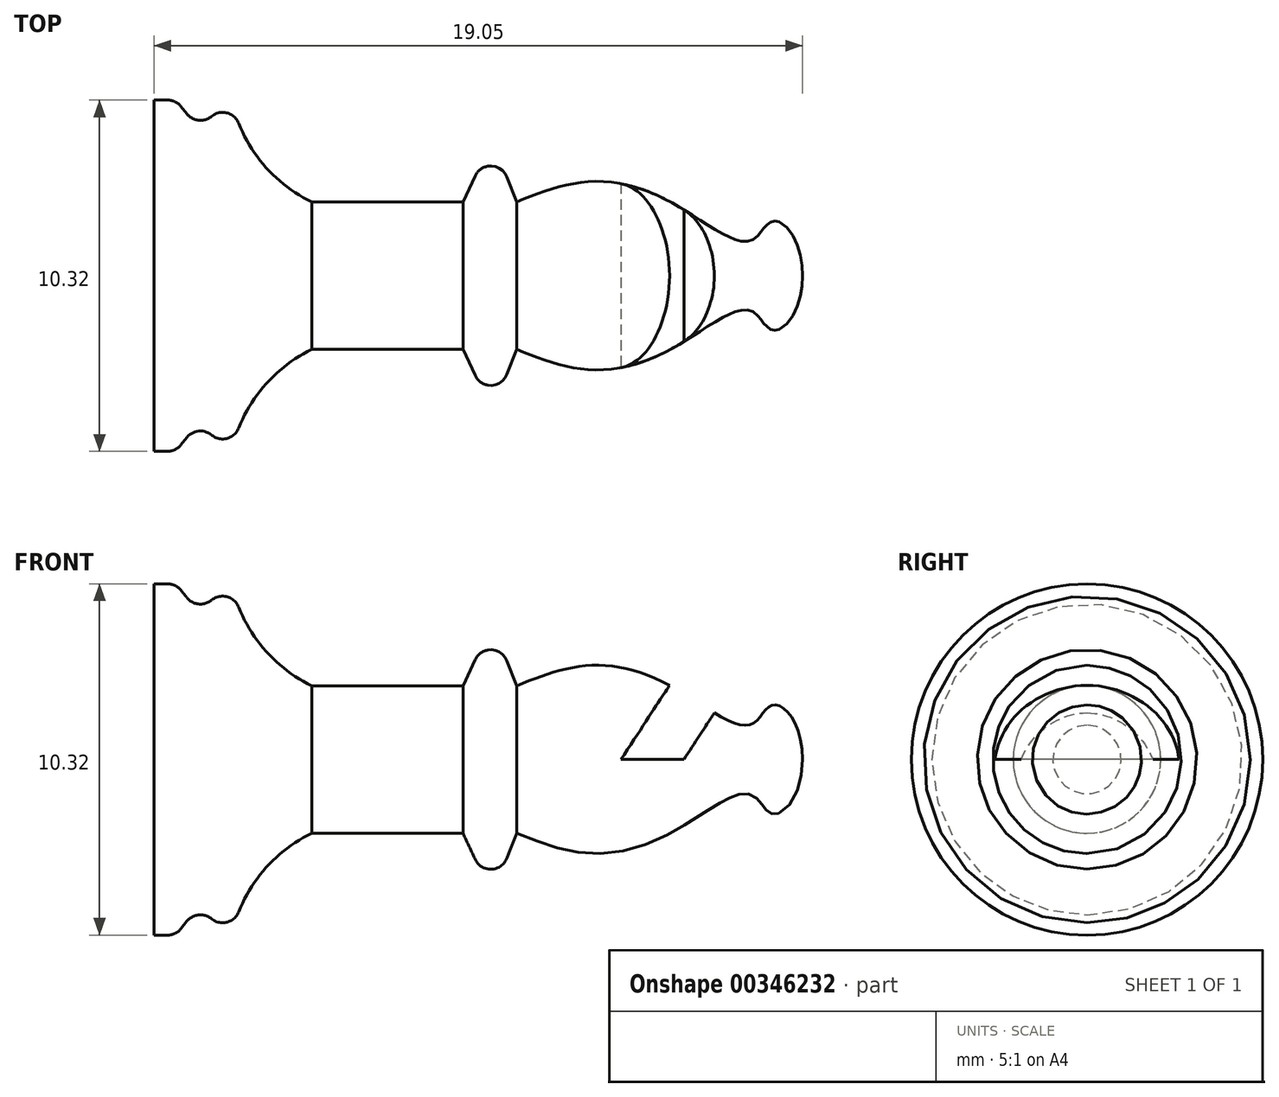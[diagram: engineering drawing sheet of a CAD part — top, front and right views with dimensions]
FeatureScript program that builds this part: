
annotation { "Feature Type Name" : "Feature", "Feature Type Description" : "" }
export const myFeature = defineFeature(function(context is Context, id is Id, definition is map)
    precondition{}
    {
        {
            var Q0;
            Q0=qCreatedBy(makeId("Front.planeOp"),FACE);
            var sketch = newSketch(context, id + "F0", { "sketchPlane" : qUnion([Q0])});
            skLineSegment(sketch, "E0", {"start": v(0, 0) * mm, "end": v(-19.05, 0) * mm});
            skLineSegment(sketch, "E1", {"start": v(-19.05, 0) * mm, "end": v(-19.05, 5.16) * mm});
            skLineSegment(sketch, "E2", {"start": v(-19.05, 5.16) * mm, "end": v(-18.41, 5.16) * mm});
            skLineSegment(sketch, "E3", {"start": v(-18.41, 5.16) * mm, "end": v(-17.76, 4.36) * mm});
            skLineSegment(sketch, "E4", {"start": v(-17.76, 4.36) * mm, "end": v(-16.77, 5.16) * mm});
            skArc(sketch, "E5", {"start": v(-16.77, 5.16) * mm, "mid": v(-15.94, 3.4) * mm, "end": v(-14.42, 2.17) * mm});
            skLineSegment(sketch, "E6", {"start": v(-14.42, 2.17) * mm, "end": v(-9.97, 2.17) * mm});
            skLineSegment(sketch, "E7", {"start": v(-9.97, 2.17) * mm, "end": v(-9.12, 4) * mm});
            skLineSegment(sketch, "E8", {"start": v(-9.12, 4) * mm, "end": v(-8.39, 2.17) * mm});
            skFitSpline(sketch, "E9", {"points": [v(-8.39, 2.17) * mm, v(-6.38, 2.76) * mm, v(-3.88, 2.17) * mm, v(-1.54, 1.02) * mm, v(-0.9, 1.6) * mm, v(0, 0) * mm], "startDerivative": vector(9.4, 3.76) * mm, "endDerivative": vector(0, -16.76) * mm});
            skSolve(sketch);
        }
        {
            var Q0;
            Q0=makeQuery(id+"F0.imprint","IMPRINT",FACE,{"disambiguationData":[TD([[makeQuery(id+"F0.imprint","IMPRINT",EDGE,{"derivedFrom":sQuery(id+"F0.wireOp",EDGE,"E0")}),-1.0]])]});
            var Q1;
            Q1=sQuery(id+"F0.wireOp",EDGE,"E0");
            revolve(context, id + "F1", {"entities" : qUnion([Q0]), "axis" : qUnion([Q1]), "revolveType" : RevolveType.FULL});
        }
        {
            var Q0;
            Q0=makeQuery(id+"F1.opRevolve","SWEPT_EDGE",EDGE,{"disambiguationData":[OSD([sQuery(id+"F0.wireOp",EDGE,"E7"),sQuery(id+"F0.wireOp",EDGE,"E8")])]});
            var Q1;
            Q1=makeQuery(id+"F1.opRevolve","SWEPT_EDGE",EDGE,{"disambiguationData":[OSD([sQuery(id+"F0.wireOp",EDGE,"AUx2sYwA-PIeI-d8Dh-zgte-X192royZ0Wcn"),sQuery(id+"F0.wireOp",EDGE,"91591d6d-3b99-44fd-bbde-36bfa9a7b408")])]});
            var Q2;
            Q2=makeQuery(id+"F1.opRevolve","SWEPT_EDGE",EDGE,{"disambiguationData":[OSD([sQuery(id+"F0.wireOp",EDGE,"E4"),sQuery(id+"F0.wireOp",EDGE,"E5")])]});
            var Q3;
            Q3=makeQuery(id+"F1.opRevolve","SWEPT_EDGE",EDGE,{"disambiguationData":[OSD([sQuery(id+"F0.wireOp",EDGE,"E2"),sQuery(id+"F0.wireOp",EDGE,"E3")])]});
            var Q4;
            Q4=makeQuery(id+"F1.opRevolve","SWEPT_EDGE",EDGE,{"disambiguationData":[OSD([sQuery(id+"F0.wireOp",EDGE,"E3"),sQuery(id+"F0.wireOp",EDGE,"E4")])]});
            fillet(context, id + "F2", {"entities" : qUnion([Q0, Q1, Q2, Q3, Q4]), "radius" : 0.5 * mm, "tangentPropagation" : true, "allowEdgeOverflow" : false});
        }
        {
            var Q0;
            Q0=qCreatedBy(makeId("Front.planeOp"),FACE);
            var sketch = newSketch(context, id + "F3", { "sketchPlane" : qUnion([Q0])});
            skLineSegment(sketch, "E10", {"start": v(-5.33, 0) * mm, "end": v(-3.23, 3.22) * mm});
            skLineSegment(sketch, "E11", {"start": v(-3.23, 3.22) * mm, "end": v(-1.93, 2.37) * mm});
            skLineSegment(sketch, "E12", {"start": v(-1.93, 2.37) * mm, "end": v(-3.49, 0) * mm});
            skLineSegment(sketch, "E13", {"start": v(-3.49, 0) * mm, "end": v(-5.33, 0) * mm});
            skSolve(sketch);
        }
        {
            var Q0;
            Q0=makeQuery(id+"F3.imprint","IMPRINT",FACE,{"disambiguationData":[TD([[makeQuery(id+"F3.imprint","IMPRINT",EDGE,{"derivedFrom":sQuery(id+"F3.wireOp",EDGE,"E10")}),-1.0]])]});
            extrude(context, id + "F4", {"entities" : qUnion([Q0]), "operationType" : NewBodyOperationType.REMOVE, "endBound" : BoundingType.SYMMETRIC, "oppositeDirection" : true, "depth" : 25.4 * mm});
        }
    });
